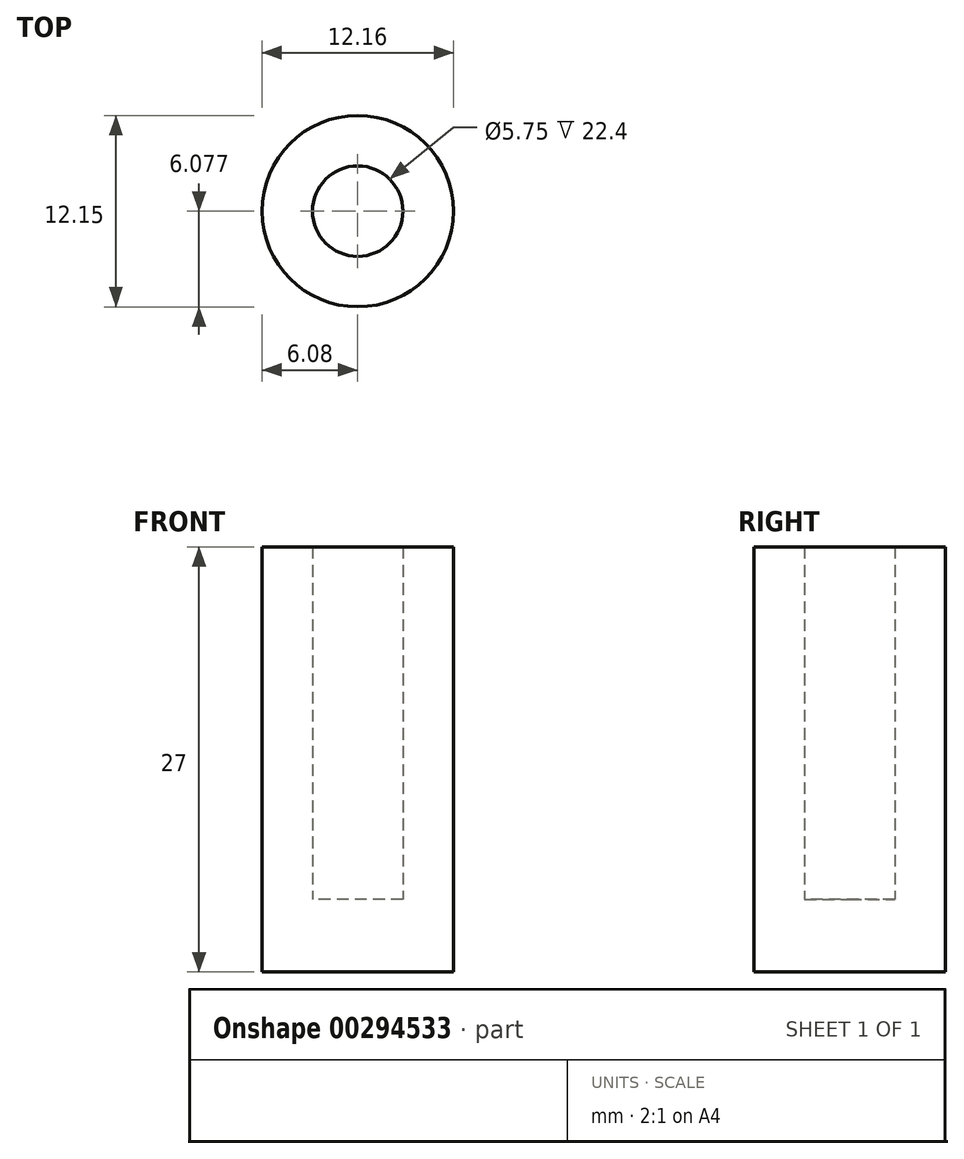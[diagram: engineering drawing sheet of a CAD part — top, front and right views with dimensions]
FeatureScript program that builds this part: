
annotation { "Feature Type Name" : "Feature", "Feature Type Description" : "" }
export const myFeature = defineFeature(function(context is Context, id is Id, definition is map)
    precondition{}
    {
        {
            var Q0;
            Q0=qCreatedBy(makeId("Top.planeOp"),FACE);
            var sketch = newSketch(context, id + "F0", { "sketchPlane" : qUnion([Q0])});
            skLineSegment(sketch, "E0.bottom", {"start": v(-10.83, 9.45) * mm, "end": v(0, 13.63) * mm});
            skLineSegment(sketch, "E0.top", {"start": v(-10.83, 21.57) * mm, "end": v(0, 21.57) * mm});
            skLineSegment(sketch, "E0.left", {"start": v(-10.83, 9.45) * mm, "end": v(-10.83, 21.57) * mm});
            skLineSegment(sketch, "E0.right", {"start": v(0, 13.63) * mm, "end": v(0, 21.57) * mm});
            skLineSegment(sketch, "E1", {"start": v(-33.01, 18.6) * mm, "end": v(-17.2, 18.3) * mm});
            skLineSegment(sketch, "E2", {"start": v(-17.2, 18.3) * mm, "end": v(-16.35, -1.4) * mm});
            skLineSegment(sketch, "E3", {"start": v(-16.35, -1.4) * mm, "end": v(-33.01, -1.4) * mm});
            skLineSegment(sketch, "E4", {"start": v(-33.01, -1.4) * mm, "end": v(-33.01, 18.6) * mm});
            skFitSpline(sketch, "E5", {"points": [v(-17.2, 18.3) * mm, v(-12.43, 13.75) * mm, v(-9.04, 15.88) * mm, v(-6.03, 19.56) * mm, v(-10.83, 21.57) * mm], "startDerivative": vector(17.19, -23.41) * mm, "endDerivative": vector(25.6, -4.04) * mm});
            skCircle(sketch, "E6", {"center": v(43.86, 10.29) * mm, "radius": 2.87 * mm});
            skCircle(sketch, "E7.0", {"center": v(43.86, 10.29) * mm, "radius": 6.08 * mm});
            skCircle(sketch, "E8.0", {"center": v(43.86, 10.29) * mm, "radius": 16.08 * mm});
            skCircle(sketch, "E9.0", {"center": v(43.86, 10.29) * mm, "radius": 21.08 * mm});
            skSolve(sketch);
        }
        {
            var Q0;
            Q0=makeQuery(id+"F0.imprint","IMPRINT",FACE,{"disambiguationData":[TD([[makeQuery(id+"F0.imprint","IMPRINT",EDGE,{"derivedFrom":sQuery(id+"F0.wireOp",EDGE,"E8.0")}),-1.0]])]});
            var Q1;
            Q1=makeQuery(id+"F0.imprint","IMPRINT",FACE,{"disambiguationData":[TD([[makeQuery(id+"F0.imprint","IMPRINT",EDGE,{"derivedFrom":sQuery(id+"F0.wireOp",EDGE,"E7.0")}),1.0]])]});
            var Q2;
            Q2=makeQuery(id+"F0.imprint","IMPRINT",FACE,{"disambiguationData":[TD([[makeQuery(id+"F0.imprint","IMPRINT",EDGE,{"derivedFrom":sQuery(id+"F0.wireOp",EDGE,"E6")}),1.0]])]});
            var Q3;
            Q3=makeQuery(id+"F0.imprint","IMPRINT",FACE,{"disambiguationData":[TD([[makeQuery(id+"F0.imprint","IMPRINT",EDGE,{"derivedFrom":sQuery(id+"F0.wireOp",EDGE,"E6")}),-1.0]])]});
            var Q4;
            Q4=sQuery(id+"F0.wireOp",EDGE,"E9.0");
            var Q5;
            Q5=sQuery(id+"F0.wireOp",EDGE,"E8.0");
            extrude(context, id + "F1", {"entities" : qUnion([Q0, Q1, Q2, Q3]), "surfaceEntities" : qUnion([Q4, Q5]), "depth" : 4.6 * mm});
        }
        {
            var Q0;
            Q0=makeQuery(id+"F0.imprint","IMPRINT",FACE,{"disambiguationData":[TD([[makeQuery(id+"F0.imprint","IMPRINT",EDGE,{"derivedFrom":sQuery(id+"F0.wireOp",EDGE,"E7.0")}),1.0]])]});
            extrude(context, id + "F2", {"entities" : qUnion([Q0]), "operationType" : NewBodyOperationType.ADD, "depth" : 27 * mm});
        }
        {
            var Q0;
            Q0=makeQuery(id+"F2.boolean.opBoolean","SPLIT",FACE,{"disambiguationData":[TD([makeQuery(id+"F2.opExtrude","SWEPT_FACE",FACE,{"disambiguationData":[OSD([sQuery(id+"F0.wireOp",EDGE,"E7.0")])]})])],"derivedFrom":makeQuery(id+"F1.opExtrude","CAP_FACE",FACE,{"disambiguationData":[OSD([sQuery(id+"F0.wireOp",EDGE,"E9.0")])],"isStart":false})});
            extrude(context, id + "F3", {"entities" : qUnion([Q0]), "operationType" : NewBodyOperationType.REMOVE, "oppositeDirection" : true, "depth" : 25 * mm});
        }
    });
